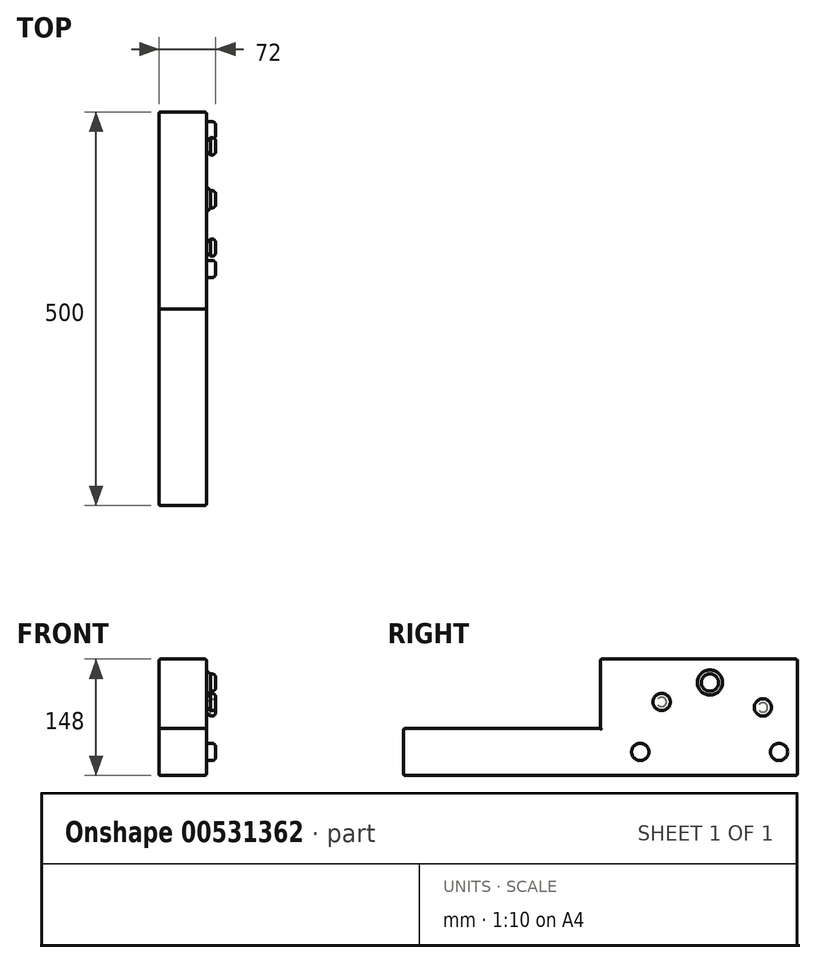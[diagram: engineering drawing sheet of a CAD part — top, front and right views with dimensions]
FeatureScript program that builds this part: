
annotation { "Feature Type Name" : "Feature", "Feature Type Description" : "" }
export const myFeature = defineFeature(function(context is Context, id is Id, definition is map)
    precondition{}
    {
        {
            var Q0;
            Q0=qCreatedBy(makeId("Top.planeOp"),FACE);
            var sketch = newSketch(context, id + "F0", { "sketchPlane" : qUnion([Q0])});
            skLineSegment(sketch, "E0.bottom", {"start": v(0, 0) * mm, "end": v(60, 0) * mm});
            skLineSegment(sketch, "E0.top", {"start": v(0, 500) * mm, "end": v(60, 500) * mm});
            skLineSegment(sketch, "E0.left", {"start": v(0, 0) * mm, "end": v(0, 500) * mm});
            skLineSegment(sketch, "E0.right", {"start": v(60, 0) * mm, "end": v(60, 500) * mm});
            skSolve(sketch);
        }
        {
            var Q0;
            Q0=makeQuery(id+"F0.imprint","IMPRINT",FACE,{"disambiguationData":[TD([[makeQuery(id+"F0.imprint","IMPRINT",EDGE,{"derivedFrom":sQuery(id+"F0.wireOp",EDGE,"E0.bottom")}),1.0]])]});
            extrude(context, id + "F1", {"entities" : qUnion([Q0]), "depth" : 60 * mm, "offsetDistance" : 25 * mm});
        }
        {
            var Q0;
            Q0=makeQuery(id+"F1.opExtrude","SWEPT_FACE",FACE,{"disambiguationData":[OSD([sQuery(id+"F0.wireOp",EDGE,"E0.right")])]});
            var sketch = newSketch(context, id + "F2", { "sketchPlane" : qUnion([Q0])});
            skCircle(sketch, "E1", {"center": v(476.82, 30) * mm, "radius": 11 * mm});
            skPoint(sketch, "E1.centerSnap0", {"position": v(500, 30) * mm});
            skCircle(sketch, "E2", {"center": v(389.12, 30) * mm, "radius": 100 * mm, "construction": true});
            skCircle(sketch, "E3", {"center": v(389.12, 118.17) * mm, "radius": 11 * mm});
            skCircle(sketch, "E4", {"center": v(300.57, 30) * mm, "radius": 11 * mm});
            skSolve(sketch);
        }
        {
            var Q0;
            Q0=makeQuery(id+"F2.imprint","IMPRINT",FACE,{"disambiguationData":[TD([[makeQuery(id+"F2.imprint","IMPRINT",EDGE,{"derivedFrom":sQuery(id+"F2.wireOp",EDGE,"E4")}),1.0]])]});
            var Q1;
            Q1=makeQuery(id+"F2.imprint","IMPRINT",FACE,{"disambiguationData":[TD([[makeQuery(id+"F2.imprint","IMPRINT",EDGE,{"derivedFrom":sQuery(id+"F2.wireOp",EDGE,"E3")}),1.0]])]});
            var Q2;
            Q2=makeQuery(id+"F2.imprint","IMPRINT",FACE,{"disambiguationData":[TD([[makeQuery(id+"F2.imprint","IMPRINT",EDGE,{"derivedFrom":sQuery(id+"F2.wireOp",EDGE,"E1")}),1.0]])]});
            var Q3;
            Q3=sQuery(id+"F2.wireOp",EDGE,"E3");
            var Q4;
            Q4=sQuery(id+"F2.wireOp",EDGE,"E4");
            var Q5;
            Q5=sQuery(id+"F2.wireOp",EDGE,"E1");
            extrude(context, id + "F3", {"entities" : qUnion([Q0, Q1, Q2]), "surfaceEntities" : qUnion([Q3, Q4, Q5]), "depth" : 12 * mm, "offsetDistance" : 25 * mm});
        }
        {
            var Q0;
            Q0=makeQuery(id+"F1.opExtrude","CAP_FACE",FACE,{"disambiguationData":[OSD([sQuery(id+"F0.wireOp",EDGE,"E0.bottom"),sQuery(id+"F0.wireOp",EDGE,"E0.top"),sQuery(id+"F0.wireOp",EDGE,"E0.left"),sQuery(id+"F0.wireOp",EDGE,"E0.right")])],"isStart":true});
            var sketch = newSketch(context, id + "F4", { "sketchPlane" : qUnion([Q0])});
            skLineSegment(sketch, "E5.bottom", {"start": v(0, -500) * mm, "end": v(60, -500) * mm});
            skLineSegment(sketch, "E5.top", {"start": v(0, -250) * mm, "end": v(60, -250) * mm});
            skLineSegment(sketch, "E5.left", {"start": v(0, -500) * mm, "end": v(0, -250) * mm});
            skLineSegment(sketch, "E5.right", {"start": v(60, -500) * mm, "end": v(60, -250) * mm});
            skPoint(sketch, "E5.middle", {"position": v(30, -375) * mm});
            skPoint(sketch, "E5.middle.positionSnap0", {"position": v(30, -500) * mm});
            skPoint(sketch, "E5.centerSnap0", {"position": v(30, -500) * mm});
            skSolve(sketch);
        }
        {
            var Q0;
            Q0=makeQuery(id+"F4.imprint","IMPRINT",FACE,{"disambiguationData":[TD([[makeQuery(id+"F4.imprint","IMPRINT",EDGE,{"derivedFrom":sQuery(id+"F4.wireOp",EDGE,"E5.bottom")}),1.0]])]});
            var Q1;
            Q1=sQuery(id+"F4.wireOp",EDGE,"E5.left");
            var Q2;
            Q2=sQuery(id+"F4.wireOp",EDGE,"E5.top");
            var Q3;
            Q3=sQuery(id+"F4.wireOp",EDGE,"E5.right");
            var Q4;
            Q4=sQuery(id+"F4.wireOp",EDGE,"E5.bottom");
            extrude(context, id + "F5", {"entities" : qUnion([Q0]), "operationType" : NewBodyOperationType.ADD, "surfaceEntities" : qUnion([Q1, Q2, Q3, Q4]), "oppositeDirection" : true, "depth" : 148 * mm, "offsetDistance" : 25 * mm});
        }
        {
            var Q0;
            Q0=makeQuery(id+"F5.boolean.opBoolean","MERGE",FACE,{"derivedFrom":[makeQuery(id+"F1.opExtrude","SWEPT_FACE",FACE,{"disambiguationData":[OSD([sQuery(id+"F0.wireOp",EDGE,"E0.right")])]}),makeQuery(id+"F5.opExtrude","SWEPT_FACE",FACE,{"disambiguationData":[OSD([sQuery(id+"F4.wireOp",EDGE,"E5.right")])]})]});
            var sketch = newSketch(context, id + "F6", { "sketchPlane" : qUnion([Q0])});
            skCircle(sketch, "E6", {"center": v(327.76, 93.53) * mm, "radius": 11 * mm});
            skCircle(sketch, "E7", {"center": v(456.35, 86.57) * mm, "radius": 11 * mm});
            skSolve(sketch);
        }
        {
            var Q0;
            Q0=makeQuery(id+"F6.imprint","IMPRINT",FACE,{"disambiguationData":[TD([[makeQuery(id+"F6.imprint","IMPRINT",EDGE,{"derivedFrom":sQuery(id+"F6.wireOp",EDGE,"E6")}),1.0]])]});
            var Q1;
            Q1=makeQuery(id+"F6.imprint","IMPRINT",FACE,{"disambiguationData":[TD([[makeQuery(id+"F6.imprint","IMPRINT",EDGE,{"derivedFrom":sQuery(id+"F6.wireOp",EDGE,"E7")}),1.0]])]});
            var Q2;
            Q2=sQuery(id+"F6.wireOp",EDGE,"E6");
            var Q3;
            Q3=sQuery(id+"F6.wireOp",EDGE,"E7");
            extrude(context, id + "F7", {"entities" : qUnion([Q0, Q1]), "surfaceEntities" : qUnion([Q2, Q3]), "depth" : 12 * mm, "offsetDistance" : 25 * mm});
        }
        {
            var Q0;
            Q0=makeQuery(id+"F1.opExtrude","CAP_EDGE",EDGE,{"disambiguationData":[OSD([sQuery(id+"F0.wireOp",EDGE,"E0.right")])],"isStart":false});
            var Q1;
            Q1=makeQuery(id+"F1.opExtrude","SWEPT_EDGE",EDGE,{"disambiguationData":[OSD([sQuery(id+"F0.wireOp",EDGE,"E0.bottom"),sQuery(id+"F0.wireOp",EDGE,"E0.right")])]});
            var Q2;
            Q2=makeQuery(id+"F1.opExtrude","CAP_EDGE",EDGE,{"disambiguationData":[OSD([sQuery(id+"F0.wireOp",EDGE,"E0.right")])],"isStart":true});
            var Q3;
            Q3=makeQuery(id+"F5.opExtrude","SWEPT_EDGE",EDGE,{"disambiguationData":[OSD([sQuery(id+"F0.wireOp",EDGE,"E0.right"),sQuery(id+"F4.wireOp",EDGE,"E5.top"),sQuery(id+"F4.wireOp",EDGE,"E5.right")])]});
            var Q4;
            Q4=makeQuery(id+"F5.opExtrude","CAP_EDGE",EDGE,{"disambiguationData":[OSD([sQuery(id+"F4.wireOp",EDGE,"E5.right")])],"isStart":false});
            var Q5;
            Q5=makeQuery(id+"F5.boolean.opBoolean","MERGE",EDGE,{"derivedFrom":[makeQuery(id+"F1.opExtrude","SWEPT_EDGE",EDGE,{"disambiguationData":[OSD([sQuery(id+"F0.wireOp",EDGE,"E0.top"),sQuery(id+"F0.wireOp",EDGE,"E0.right")])]}),makeQuery(id+"F5.opExtrude","SWEPT_EDGE",EDGE,{"disambiguationData":[OSD([sQuery(id+"F4.wireOp",EDGE,"E5.bottom"),sQuery(id+"F4.wireOp",EDGE,"E5.right")])]})]});
            var Q6;
            Q6=makeQuery(id+"F1.opExtrude","CAP_EDGE",EDGE,{"disambiguationData":[OSD([sQuery(id+"F0.wireOp",EDGE,"E0.bottom")])],"isStart":true});
            var Q7;
            Q7=makeQuery(id+"F1.opExtrude","SWEPT_EDGE",EDGE,{"disambiguationData":[OSD([sQuery(id+"F0.wireOp",EDGE,"E0.bottom"),sQuery(id+"F0.wireOp",EDGE,"E0.left")])]});
            var Q8;
            Q8=makeQuery(id+"F1.opExtrude","CAP_EDGE",EDGE,{"disambiguationData":[OSD([sQuery(id+"F0.wireOp",EDGE,"E0.bottom")])],"isStart":false});
            var Q9;
            Q9=makeQuery(id+"F5.opExtrude","CAP_EDGE",EDGE,{"disambiguationData":[OSD([sQuery(id+"F4.wireOp",EDGE,"E5.top")])],"isStart":false});
            var Q10;
            Q10=makeQuery(id+"F5.opExtrude","CAP_EDGE",EDGE,{"disambiguationData":[OSD([sQuery(id+"F4.wireOp",EDGE,"E5.left")])],"isStart":false});
            var Q11;
            Q11=makeQuery(id+"F1.opExtrude","CAP_EDGE",EDGE,{"disambiguationData":[OSD([sQuery(id+"F0.wireOp",EDGE,"E0.left")])],"isStart":false});
            var Q12;
            Q12=makeQuery(id+"F5.opExtrude","SWEPT_EDGE",EDGE,{"disambiguationData":[OSD([sQuery(id+"F0.wireOp",EDGE,"E0.left"),sQuery(id+"F4.wireOp",EDGE,"E5.top"),sQuery(id+"F4.wireOp",EDGE,"E5.left")])]});
            var Q13;
            Q13=makeQuery(id+"F1.opExtrude","CAP_EDGE",EDGE,{"disambiguationData":[OSD([sQuery(id+"F0.wireOp",EDGE,"E0.left")])],"isStart":true});
            var Q14;
            Q14=makeQuery(id+"F1.opExtrude","CAP_EDGE",EDGE,{"disambiguationData":[OSD([sQuery(id+"F0.wireOp",EDGE,"E0.top")])],"isStart":true});
            var Q15;
            Q15=makeQuery(id+"F5.boolean.opBoolean","MERGE",EDGE,{"derivedFrom":[makeQuery(id+"F1.opExtrude","SWEPT_EDGE",EDGE,{"disambiguationData":[OSD([sQuery(id+"F0.wireOp",EDGE,"E0.top"),sQuery(id+"F0.wireOp",EDGE,"E0.left")])]}),makeQuery(id+"F5.opExtrude","SWEPT_EDGE",EDGE,{"disambiguationData":[OSD([sQuery(id+"F4.wireOp",EDGE,"E5.bottom"),sQuery(id+"F4.wireOp",EDGE,"E5.left")])]})]});
            var Q16;
            Q16=makeQuery(id+"F5.opExtrude","CAP_EDGE",EDGE,{"disambiguationData":[OSD([sQuery(id+"F4.wireOp",EDGE,"E5.bottom")])],"isStart":false});
            fillet(context, id + "F8", {"entities" : qUnion([Q0, Q1, Q2, Q3, Q4, Q5, Q6, Q7, Q8, Q9, Q10, Q11, Q12, Q13, Q14, Q15, Q16]), "radius" : 2 * mm, "tangentPropagation" : true, "allowEdgeOverflow" : false});
        }
        {
            var Q0;
            Q0=makeQuery(id+"F3.opExtrude","CAP_EDGE",EDGE,{"disambiguationData":[OSD([sQuery(id+"F2.wireOp",EDGE,"E4")])],"isStart":false});
            var Q1;
            Q1=makeQuery(id+"F7.opExtrude","CAP_EDGE",EDGE,{"disambiguationData":[OSD([sQuery(id+"F6.wireOp",EDGE,"E6")])],"isStart":false});
            var Q2;
            Q2=makeQuery(id+"F3.opExtrude","CAP_EDGE",EDGE,{"disambiguationData":[OSD([sQuery(id+"F2.wireOp",EDGE,"E3")])],"isStart":false});
            var Q3;
            Q3=makeQuery(id+"F3.opExtrude","CAP_EDGE",EDGE,{"disambiguationData":[OSD([sQuery(id+"F2.wireOp",EDGE,"E1")])],"isStart":false});
            var Q4;
            Q4=makeQuery(id+"F7.opExtrude","CAP_EDGE",EDGE,{"disambiguationData":[OSD([sQuery(id+"F6.wireOp",EDGE,"E7")])],"isStart":false});
            fillet(context, id + "F9", {"entities" : qUnion([Q0, Q1, Q2, Q3, Q4]), "radius" : 5 * mm, "tangentPropagation" : true, "allowEdgeOverflow" : false});
        }
        {
            var Q0;
            Q0=makeQuery(id+"F7.opExtrude","CAP_EDGE",EDGE,{"disambiguationData":[OSD([sQuery(id+"F6.wireOp",EDGE,"E6")])],"isStart":true});
            var Q1;
            Q1=makeQuery(id+"F3.opExtrude","CAP_EDGE",EDGE,{"disambiguationData":[OSD([sQuery(id+"F2.wireOp",EDGE,"E3")])],"isStart":true});
            var Q2;
            Q2=makeQuery(id+"F7.opExtrude","CAP_EDGE",EDGE,{"disambiguationData":[OSD([sQuery(id+"F6.wireOp",EDGE,"E7")])],"isStart":true});
            var Q3;
            Q3=makeQuery(id+"F3.opExtrude","CAP_EDGE",EDGE,{"disambiguationData":[OSD([sQuery(id+"F2.wireOp",EDGE,"E1")])],"isStart":true});
            var Q4;
            Q4=makeQuery(id+"F3.opExtrude","CAP_EDGE",EDGE,{"disambiguationData":[OSD([sQuery(id+"F2.wireOp",EDGE,"E4")])],"isStart":true});
            chamfer(context, id + "F10", {"entities" : qUnion([Q0, Q1, Q2, Q3, Q4]), "width" : 5 * mm, "tangentPropagation" : true});
        }
    });
